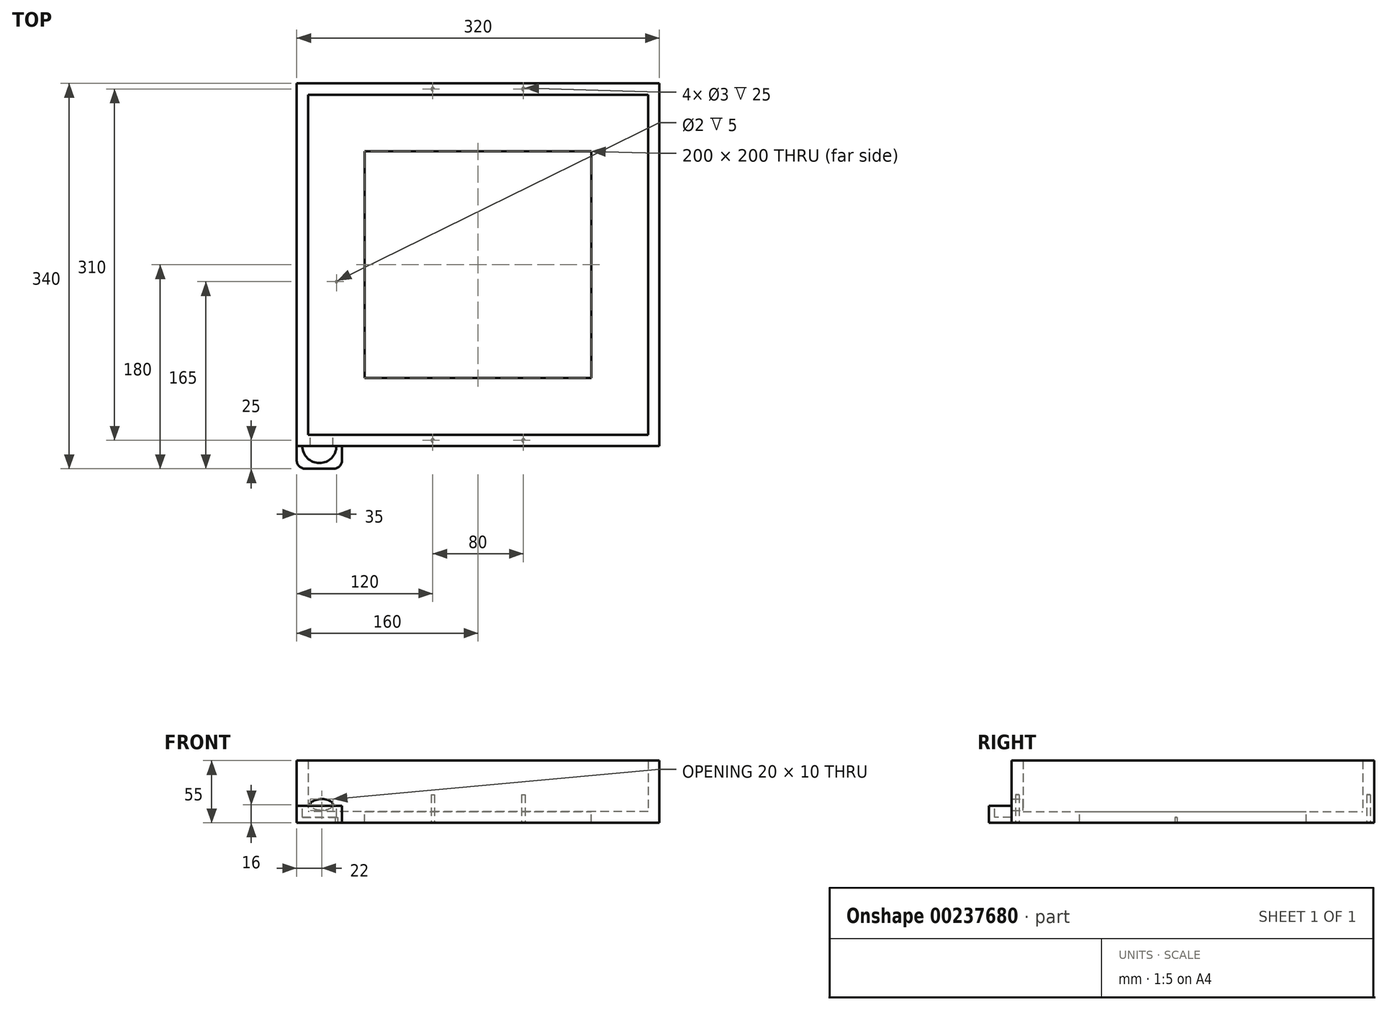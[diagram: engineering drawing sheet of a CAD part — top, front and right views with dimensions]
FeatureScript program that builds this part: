
annotation { "Feature Type Name" : "Feature", "Feature Type Description" : "" }
export const myFeature = defineFeature(function(context is Context, id is Id, definition is map)
    precondition{}
    {
        {
            var Q0;
            Q0=qCreatedBy(makeId("Top.planeOp"),FACE);
            var sketch = newSketch(context, id + "F0", { "sketchPlane" : qUnion([Q0])});
            skLineSegment(sketch, "E0.bottom", {"start": v(160, 160) * mm, "end": v(-160, 160) * mm});
            skLineSegment(sketch, "E0.top", {"start": v(160, -160) * mm, "end": v(-160, -160) * mm});
            skLineSegment(sketch, "E0.left", {"start": v(160, 160) * mm, "end": v(160, -160) * mm});
            skLineSegment(sketch, "E0.right", {"start": v(-160, 160) * mm, "end": v(-160, -160) * mm});
            skPoint(sketch, "E0.middle", {"position": v(0, 0) * mm});
            skSolve(sketch);
        }
        {
            var Q0;
            Q0 = qSketchRegion(id + "F0", true);
            extrude(context, id + "F1", {"entities" : qUnion([Q0]), "depth" : 10 * mm});
        }
        {
            var Q0;
            Q0=makeQuery(id+"F1.opExtrude","CAP_FACE",FACE,{"disambiguationData":[OSD([sQuery(id+"F0.wireOp",EDGE,"E0.bottom"),sQuery(id+"F0.wireOp",EDGE,"E0.top"),sQuery(id+"F0.wireOp",EDGE,"E0.left"),sQuery(id+"F0.wireOp",EDGE,"E0.right")])],"isStart":false});
            var sketch = newSketch(context, id + "F2", { "sketchPlane" : qUnion([Q0])});
            skLineSegment(sketch, "E1", {"start": v(-160, 160) * mm, "end": v(160, 160) * mm});
            skLineSegment(sketch, "E2", {"start": v(160, 160) * mm, "end": v(160, -160) * mm});
            skLineSegment(sketch, "E3", {"start": v(160, -160) * mm, "end": v(-160, -160) * mm});
            skLineSegment(sketch, "E4", {"start": v(-160, -160) * mm, "end": v(-160, 160) * mm});
            skLineSegment(sketch, "E5", {"start": v(-150, 150) * mm, "end": v(150, 150) * mm});
            skLineSegment(sketch, "E6", {"start": v(150, 150) * mm, "end": v(150, -150) * mm});
            skLineSegment(sketch, "E7", {"start": v(150, -150) * mm, "end": v(-150, -150) * mm});
            skLineSegment(sketch, "E8", {"start": v(-150, -150) * mm, "end": v(-150, 150) * mm});
            skSolve(sketch);
        }
        {
            var Q0;
            Q0 = qSketchRegion(id + "F2", true);
            extrude(context, id + "F3", {"entities" : qUnion([Q0]), "operationType" : NewBodyOperationType.ADD, "depth" : 45 * mm});
        }
        {
            var Q0;
            Q0=makeQuery(id+"F1.opExtrude","CAP_FACE",FACE,{"disambiguationData":[OSD([sQuery(id+"F0.wireOp",EDGE,"E0.bottom"),sQuery(id+"F0.wireOp",EDGE,"E0.top"),sQuery(id+"F0.wireOp",EDGE,"E0.left"),sQuery(id+"F0.wireOp",EDGE,"E0.right")])],"isStart":false});
            var sketch = newSketch(context, id + "F4", { "sketchPlane" : qUnion([Q0])});
            skLineSegment(sketch, "E9", {"start": v(-100, 100) * mm, "end": v(100, 100) * mm});
            skLineSegment(sketch, "E10", {"start": v(100, 100) * mm, "end": v(100, -100) * mm});
            skLineSegment(sketch, "E11", {"start": v(100, -100) * mm, "end": v(-100, -100) * mm});
            skLineSegment(sketch, "E12", {"start": v(-100, -100) * mm, "end": v(-100, 100) * mm});
            skSolve(sketch);
        }
        {
            var Q0;
            Q0 = qSketchRegion(id + "F4", true);
            extrude(context, id + "F5", {"entities" : qUnion([Q0]), "operationType" : NewBodyOperationType.REMOVE, "oppositeDirection" : true, "depth" : 25 * mm});
        }
        {
            var Q0;
            Q0=makeQuery(id+"F3.boolean.opBoolean","MERGE",FACE,{"derivedFrom":[makeQuery(id+"F1.opExtrude","SWEPT_FACE",FACE,{"disambiguationData":[OSD([sQuery(id+"F0.wireOp",EDGE,"E0.top")])]}),makeQuery(id+"F3.opExtrude","SWEPT_FACE",FACE,{"disambiguationData":[OSD([sQuery(id+"F2.wireOp",EDGE,"E3")])]})]});
            var sketch = newSketch(context, id + "F6", { "sketchPlane" : qUnion([Q0])});
            skLineSegment(sketch, "E13", {"start": v(-160, 0) * mm, "end": v(-120, 0) * mm});
            skLineSegment(sketch, "E14", {"start": v(-120, 0) * mm, "end": v(-120, 15) * mm});
            skLineSegment(sketch, "E15", {"start": v(-120, 15) * mm, "end": v(-160, 15) * mm});
            skSolve(sketch);
        }
        {
            var Q0;
            {var subQ0=sQuery(id+"F6.wireOp",EDGE,"E13");Q0=makeQuery(id+"F6.imprint","IMPRINT",FACE,{"disambiguationData":[TD([[makeQuery(id+"F6.imprint","IMPRINT",EDGE,{"derivedFrom":subQ0}),-1.0]])]});}
            extrude(context, id + "F7", {"entities" : qUnion([Q0]), "operationType" : NewBodyOperationType.ADD, "depth" : 20 * mm});
        }
        {
            var Q0;
            Q0=makeQuery(id+"F7.opExtrude","SWEPT_FACE",FACE,{"disambiguationData":[OSD([sQuery(id+"F6.wireOp",EDGE,"E15")])]});
            var sketch = newSketch(context, id + "F8", { "sketchPlane" : qUnion([Q0])});
            skLineSegment(sketch, "E16", {"start": v(-160, -180) * mm, "end": v(-140, -180) * mm});
            skArc(sketch, "E17", {"start": v(-155, -160) * mm, "mid": v(-140, -175) * mm, "end": v(-125, -160) * mm});
            skSolve(sketch);
        }
        {
            var Q0;
            {var subQ0=sQuery(id+"F8.wireOp",EDGE,"E17");Q0=makeQuery(id+"F8.imprint","IMPRINT",FACE,{"disambiguationData":[TD([[makeQuery(id+"F8.imprint","IMPRINT",EDGE,{"derivedFrom":subQ0}),1.0]])]});}
            extrude(context, id + "F9", {"entities" : qUnion([Q0]), "operationType" : NewBodyOperationType.REMOVE, "oppositeDirection" : true, "depth" : 10 * mm});
        }
        {
            var Q0;
            Q0=makeQuery(id+"F7.opExtrude","CAP_EDGE",EDGE,{"disambiguationData":[OSD([sQuery(id+"F6.wireOp",EDGE,"E14")])],"isStart":false});
            var Q1;
            Q1=makeQuery(id+"F7.opExtrude","CAP_EDGE",EDGE,{"disambiguationData":[OSD([sQuery(id+"F0.wireOp",EDGE,"E0.top"),sQuery(id+"F0.wireOp",EDGE,"E0.right"),sQuery(id+"F2.wireOp",EDGE,"E3"),sQuery(id+"F2.wireOp",EDGE,"E4")])],"isStart":false});
            fillet(context, id + "F10", {"entities" : qUnion([Q0, Q1]), "radius" : 7.5 * mm, "tangentPropagation" : true, "allowEdgeOverflow" : false});
        }
        {
            var Q0;
            Q0=makeQuery(id+"F3.opExtrude","SWEPT_FACE",FACE,{"disambiguationData":[OSD([sQuery(id+"F2.wireOp",EDGE,"E7")])]});
            var sketch = newSketch(context, id + "F11", { "sketchPlane" : qUnion([Q0])});
            skLineSegment(sketch, "E18", {"start": v(150, 10) * mm, "end": v(138, 10) * mm});
            skLineSegment(sketch, "E19", {"start": v(138, 10) * mm, "end": v(138, 16) * mm});
            skEllipse(sketch, "E20", {"center": v(138, 16) * mm, "majorRadius": 10 * mm, "minorRadius": 5 * mm, "majorAxis": v(1, 0)});
            skSolve(sketch);
        }
        {
            var Q0;
            Q0 = qSketchRegion(id + "F11", true);
            extrude(context, id + "F12", {"entities" : qUnion([Q0]), "operationType" : NewBodyOperationType.REMOVE, "oppositeDirection" : true, "depth" : 10 * mm});
        }
        {
            var Q0;
            Q0=makeQuery(id+"F7.boolean.opBoolean","MERGE",FACE,{"derivedFrom":[makeQuery(id+"F1.opExtrude","CAP_FACE",FACE,{"disambiguationData":[OSD([sQuery(id+"F0.wireOp",EDGE,"E0.bottom"),sQuery(id+"F0.wireOp",EDGE,"E0.top"),sQuery(id+"F0.wireOp",EDGE,"E0.left"),sQuery(id+"F0.wireOp",EDGE,"E0.right")])],"isStart":true}),makeQuery(id+"F7.opExtrude","SWEPT_FACE",FACE,{"disambiguationData":[OSD([sQuery(id+"F6.wireOp",EDGE,"E13")])]})]});
            var sketch = newSketch(context, id + "F13", { "sketchPlane" : qUnion([Q0])});
            skCircle(sketch, "E21", {"center": v(-40, 155) * mm, "radius": 1.5 * mm});
            skCircle(sketch, "E22", {"center": v(40, 155) * mm, "radius": 1.5 * mm});
            skCircle(sketch, "E23", {"center": v(40, -155) * mm, "radius": 1.5 * mm});
            skCircle(sketch, "E24", {"center": v(-40, -155) * mm, "radius": 1.5 * mm});
            skSolve(sketch);
        }
        {
            var Q0;
            Q0 = qSketchRegion(id + "F13", true);
            extrude(context, id + "F14", {"entities" : qUnion([Q0]), "operationType" : NewBodyOperationType.REMOVE, "oppositeDirection" : true, "depth" : 25 * mm});
        }
        {
            var Q0;
            Q0=makeQuery(id+"F7.boolean.opBoolean","MERGE",FACE,{"derivedFrom":[makeQuery(id+"F1.opExtrude","CAP_FACE",FACE,{"disambiguationData":[OSD([sQuery(id+"F0.wireOp",EDGE,"E0.bottom"),sQuery(id+"F0.wireOp",EDGE,"E0.top"),sQuery(id+"F0.wireOp",EDGE,"E0.left"),sQuery(id+"F0.wireOp",EDGE,"E0.right")])],"isStart":true}),makeQuery(id+"F7.opExtrude","SWEPT_FACE",FACE,{"disambiguationData":[OSD([sQuery(id+"F6.wireOp",EDGE,"E13")])]})]});
            var sketch = newSketch(context, id + "F15", { "sketchPlane" : qUnion([Q0])});
            skCircle(sketch, "E25", {"center": v(-125, 15) * mm, "radius": 1 * mm});
            skSolve(sketch);
        }
        {
            var Q0;
            Q0 = qSketchRegion(id + "F15", true);
            extrude(context, id + "F16", {"entities" : qUnion([Q0]), "operationType" : NewBodyOperationType.REMOVE, "oppositeDirection" : true, "depth" : 5 * mm});
        }
    });
